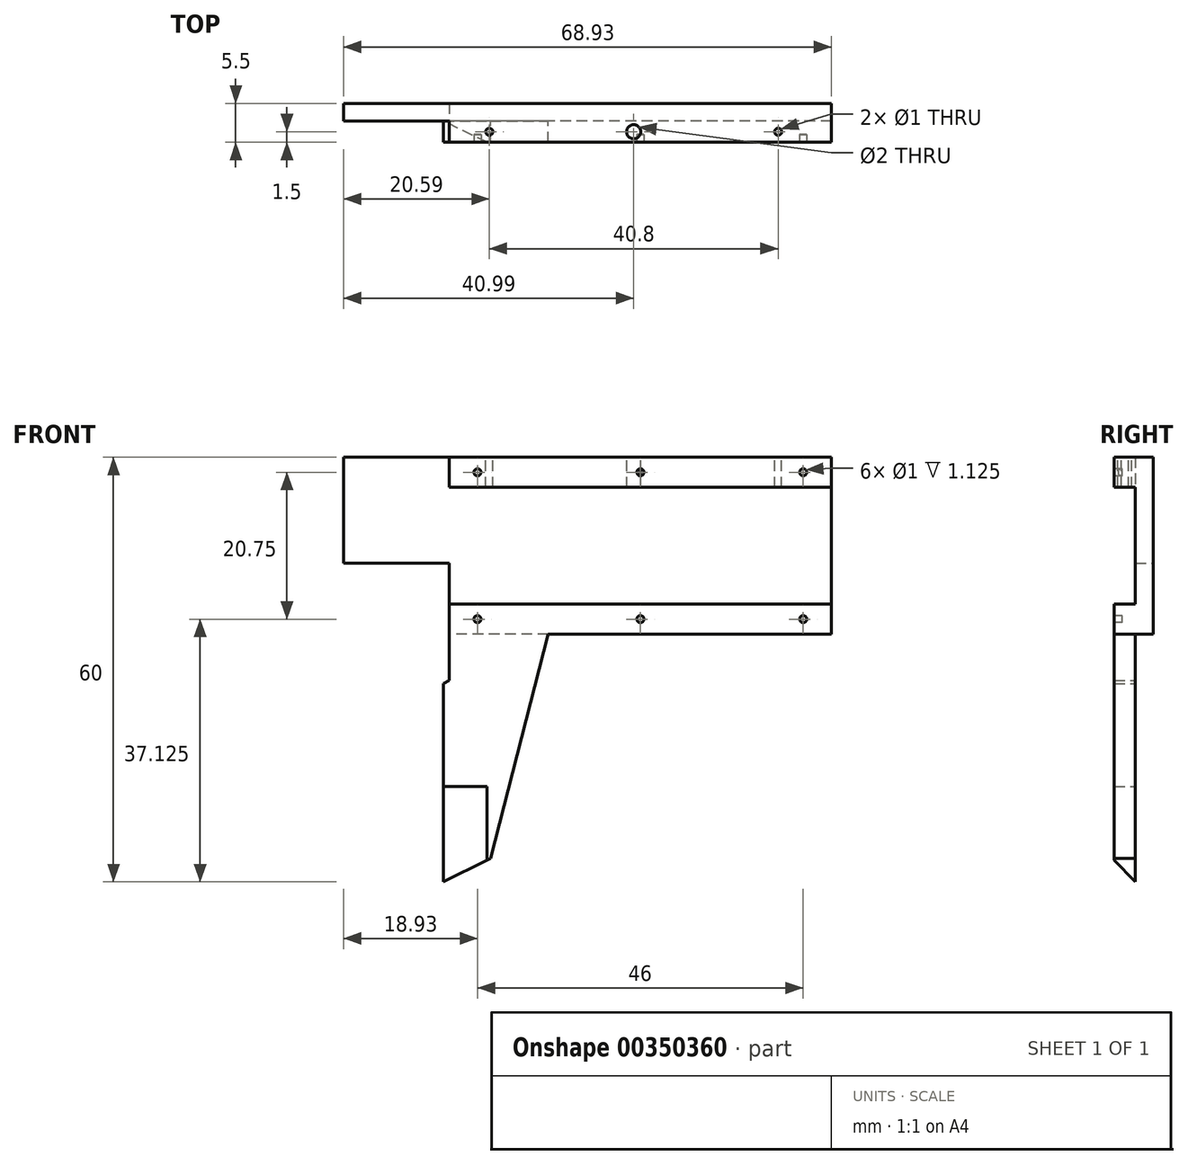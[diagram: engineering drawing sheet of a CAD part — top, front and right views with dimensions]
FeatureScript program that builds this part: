
annotation { "Feature Type Name" : "Feature", "Feature Type Description" : "" }
export const myFeature = defineFeature(function(context is Context, id is Id, definition is map)
    precondition{}
    {
        {
            var Q0;
            Q0=qCreatedBy(makeId("Front.planeOp"),FACE);
            var sketch = newSketch(context, id + "F0", { "sketchPlane" : qUnion([Q0])});
            skLineSegment(sketch, "E0", {"start": v(0, 0) * mm, "end": v(-55.4, 0) * mm, "construction": true});
            skLineSegment(sketch, "E1", {"start": v(0, 12.5) * mm, "end": v(0, -12.5) * mm});
            skLineSegment(sketch, "E2", {"start": v(0, -12.5) * mm, "end": v(-40, -12.5) * mm});
            skLineSegment(sketch, "E3", {"start": v(-40, -12.5) * mm, "end": v(-48.17, -44.18) * mm});
            skLineSegment(sketch, "E4", {"start": v(-48.17, -44.18) * mm, "end": v(-54.8, -47.5) * mm});
            skLineSegment(sketch, "E5", {"start": v(-54.8, -47.5) * mm, "end": v(-54.8, -19.5) * mm});
            skLineSegment(sketch, "E6", {"start": v(-54.8, -19.5) * mm, "end": v(-54, -19.04) * mm});
            skLineSegment(sketch, "E7", {"start": v(-54, -19.04) * mm, "end": v(-54, -2.5) * mm});
            skLineSegment(sketch, "E8", {"start": v(-54, -2.5) * mm, "end": v(-68.93, -2.5) * mm});
            skLineSegment(sketch, "E9", {"start": v(0, 12.5) * mm, "end": v(-68.93, 12.5) * mm});
            skLineSegment(sketch, "E10", {"start": v(-68.93, 12.5) * mm, "end": v(-68.93, -2.5) * mm});
            skSolve(sketch);
        }
        {
            var Q0;
            Q0=qSketchRegion(id+"F0",true);
            extrude(context, id + "F1", {"entities" : qUnion([Q0]), "depth" : 5.5 * mm});
        }
        {
            var Q0;
            Q0=makeQuery(id+"F1.opExtrude","CAP_FACE",FACE,{"disambiguationData":[OSD([sQuery(id+"F0.wireOp",EDGE,"E1"),sQuery(id+"F0.wireOp",EDGE,"E2"),sQuery(id+"F0.wireOp",EDGE,"E3"),sQuery(id+"F0.wireOp",EDGE,"E4"),sQuery(id+"F0.wireOp",EDGE,"E5"),sQuery(id+"F0.wireOp",EDGE,"E6"),sQuery(id+"F0.wireOp",EDGE,"E7"),sQuery(id+"F0.wireOp",EDGE,"E8"),sQuery(id+"F0.wireOp",EDGE,"ps4h69ml-JGIz-fiXX-pNhC-RlthW3Jydgdh"),sQuery(id+"F0.wireOp",EDGE,"E9"),sQuery(id+"F0.wireOp",EDGE,"95Vc8VKD-sbNP-E8sn-toB8-PwlkbplALVXU"),sQuery(id+"F0.wireOp",EDGE,"v8oIzNfV-Wtr4-p2Ou-QnUo-0IRdxmqncbtp"),sQuery(id+"F0.wireOp",EDGE,"jtS7aXSn-cF8S-vqdd-pwNP-jGzUUDwUnf9m"),sQuery(id+"F0.wireOp",EDGE,"i4UCeh58-nwjS-PbdF-TUSo-CF3E2kTPfbWW")])],"isStart":false});
            var sketch = newSketch(context, id + "F2", { "sketchPlane" : qUnion([Q0])});
            skLineSegment(sketch, "E11", {"start": v(0, 8.25) * mm, "end": v(0, -8.25) * mm});
            skLineSegment(sketch, "E12", {"start": v(0, -8.25) * mm, "end": v(-54, -8.25) * mm});
            skLineSegment(sketch, "E13", {"start": v(-54, -8.25) * mm, "end": v(-54, -2.5) * mm});
            skLineSegment(sketch, "E14", {"start": v(-54, -2.5) * mm, "end": v(-73.78, -2.5) * mm});
            skLineSegment(sketch, "E15", {"start": v(-73.78, -2.5) * mm, "end": v(-73.78, 31.93) * mm});
            skLineSegment(sketch, "E16", {"start": v(-73.78, 31.93) * mm, "end": v(-54, 31.93) * mm});
            skLineSegment(sketch, "E17", {"start": v(-54, 31.93) * mm, "end": v(-54, 8.25) * mm});
            skLineSegment(sketch, "E18", {"start": v(-54, 8.25) * mm, "end": v(0, 8.25) * mm});
            skSolve(sketch);
        }
        {
            var Q0;
            Q0=qSketchRegion(id+"F2",true);
            extrude(context, id + "F3", {"entities" : qUnion([Q0]), "operationType" : NewBodyOperationType.REMOVE, "oppositeDirection" : true, "depth" : 3 * mm});
        }
        {
            var Q0;
            {var subQ0=sQuery(id+"F0.wireOp",EDGE,"E1");var subQ1=sQuery(id+"F0.wireOp",EDGE,"E9");Q0=makeQuery(id+"F3.boolean.opBoolean","SPLIT",FACE,{"disambiguationData":[TD([makeQuery(id+"F1.opExtrude","SWEPT_FACE",FACE,{"disambiguationData":[OSD([subQ1])]})])],"derivedFrom":makeQuery(id+"F1.opExtrude","CAP_FACE",FACE,{"disambiguationData":[OSD([subQ0,sQuery(id+"F0.wireOp",EDGE,"E2"),sQuery(id+"F0.wireOp",EDGE,"E3"),sQuery(id+"F0.wireOp",EDGE,"E4"),sQuery(id+"F0.wireOp",EDGE,"E5"),sQuery(id+"F0.wireOp",EDGE,"E6"),sQuery(id+"F0.wireOp",EDGE,"E7"),sQuery(id+"F0.wireOp",EDGE,"E8"),sQuery(id+"F0.wireOp",EDGE,"ps4h69ml-JGIz-fiXX-pNhC-RlthW3Jydgdh"),subQ1,sQuery(id+"F0.wireOp",EDGE,"95Vc8VKD-sbNP-E8sn-toB8-PwlkbplALVXU"),sQuery(id+"F0.wireOp",EDGE,"v8oIzNfV-Wtr4-p2Ou-QnUo-0IRdxmqncbtp"),sQuery(id+"F0.wireOp",EDGE,"jtS7aXSn-cF8S-vqdd-pwNP-jGzUUDwUnf9m"),sQuery(id+"F0.wireOp",EDGE,"i4UCeh58-nwjS-PbdF-TUSo-CF3E2kTPfbWW")])],"isStart":false})});}
            var sketch = newSketch(context, id + "F4", { "sketchPlane" : qUnion([Q0])});
            skLineSegment(sketch, "E19", {"start": v(0, 0) * mm, "end": v(-25.2, 0) * mm, "construction": true});
            skCircle(sketch, "E20", {"center": v(-4, 10.38) * mm, "radius": 0.5 * mm});
            skCircle(sketch, "E21", {"center": v(-27, 10.38) * mm, "radius": 0.5 * mm});
            skCircle(sketch, "E22", {"center": v(-50, 10.37) * mm, "radius": 0.5 * mm});
            skCircle(sketch, "E23.MirrorC", {"center": v(-50, -10.38) * mm, "radius": 0.5 * mm});
            skCircle(sketch, "E24.MirrorC", {"center": v(-27, -10.38) * mm, "radius": 0.5 * mm});
            skCircle(sketch, "E25.MirrorC", {"center": v(-4, -10.38) * mm, "radius": 0.5 * mm});
            skSolve(sketch);
        }
        {
            var Q0;
            Q0=qSketchRegion(id+"F4",true);
            extrude(context, id + "F5", {"entities" : qUnion([Q0]), "operationType" : NewBodyOperationType.REMOVE, "oppositeDirection" : true, "depth" : 1.12 * mm});
        }
        {
            var Q0;
            Q0=makeQuery(id+"F1.opExtrude","SWEPT_FACE",FACE,{"disambiguationData":[OSD([sQuery(id+"F0.wireOp",EDGE,"E9")])]});
            cPlane(context, id + "F6", {"entities" : qUnion([Q0]), "cplaneType" : CPlaneType.OFFSET, "offset" : 17.5 * mm, "width" : 150 * mm, "height" : 150 * mm});
        }
        {
            var Q0;
            Q0=makeQuery(id+"F1.opExtrude","SWEPT_FACE",FACE,{"disambiguationData":[OSD([sQuery(id+"F0.wireOp",EDGE,"E2")])]});
            var Q1;
            Q1=makeQuery(id+"F1.opExtrude","CAP_VERTEX",VERTEX,{"disambiguationData":[OSD([sQuery(id+"F0.wireOp",EDGE,"E4"),sQuery(id+"F0.wireOp",EDGE,"E5")])],"isStart":false});
            cPlane(context, id + "F7", {"entities" : qUnion([Q0, Q1]), "cplaneType" : CPlaneType.PLANE_POINT, "offset" : 34.75 * mm, "width" : 150 * mm, "height" : 150 * mm});
        }
        {
            var Q0;
            Q0=qCreatedBy(id+"F6.planeOp",FACE);
            var sketch = newSketch(context, id + "F8", { "sketchPlane" : qUnion([Q0])});
            skLineSegment(sketch, "E26.0", {"start": v(-62, -2.5) * mm, "end": v(-62, 0) * mm});
            skLineSegment(sketch, "E27", {"start": v(-62, 0) * mm, "end": v(-67.13, 0) * mm});
            skLineSegment(sketch, "E28", {"start": v(-67.13, 0) * mm, "end": v(-62, -2.5) * mm});
            skLineSegment(sketch, "E29", {"start": v(-62, -1.25) * mm, "end": v(-70.99, -1.25) * mm, "construction": true});
            skLineSegment(sketch, "E30.MirrorCS", {"start": v(-62, 0) * mm, "end": v(-62, -2.5) * mm});
            skSolve(sketch);
        }
        {
            var Q0;
            Q0=qSketchRegion(id+"F8",true);
            extrude(context, id + "F9", {"entities" : qUnion([Q0]), "operationType" : NewBodyOperationType.REMOVE, "oppositeDirection" : true, "depth" : 12.5 * mm});
        }
        {
            var Q0;
            Q0=makeQuery(id+"F1.opExtrude","SWEPT_FACE",FACE,{"disambiguationData":[OSD([sQuery(id+"F0.wireOp",EDGE,"E2")])]});
            var sketch = newSketch(context, id + "F10", { "sketchPlane" : qUnion([Q0])});
            skLineSegment(sketch, "E31.bottom", {"start": v(-40, 0) * mm, "end": v(-54.8, 0) * mm});
            skLineSegment(sketch, "E31.top", {"start": v(-40, 2.5) * mm, "end": v(-54.8, 2.5) * mm});
            skLineSegment(sketch, "E31.left", {"start": v(-40, 0) * mm, "end": v(-40, 2.5) * mm});
            skLineSegment(sketch, "E31.right", {"start": v(-54.8, 0) * mm, "end": v(-54.8, 2.5) * mm});
            skSolve(sketch);
        }
        {
            var Q0;
            Q0=qSketchRegion(id+"F10",true);
            extrude(context, id + "F11", {"entities" : qUnion([Q0]), "operationType" : NewBodyOperationType.REMOVE, "depth" : 47 * mm});
        }
        {
            var Q0;
            Q0=qCreatedBy(id+"F7.planeOp",FACE);
            var sketch = newSketch(context, id + "F12", { "sketchPlane" : qUnion([Q0])});
            skLineSegment(sketch, "E32.0", {"start": v(-54.8, 5.5) * mm, "end": v(-54.8, 2.5) * mm});
            skLineSegment(sketch, "E33", {"start": v(-54.8, 5.5) * mm, "end": v(-48.65, 5.5) * mm});
            skLineSegment(sketch, "E34", {"start": v(-48.65, 5.5) * mm, "end": v(-54.8, 2.5) * mm});
            skSolve(sketch);
        }
        {
            var Q0;
            Q0=qSketchRegion(id+"F12",true);
            extrude(context, id + "F13", {"entities" : qUnion([Q0]), "operationType" : NewBodyOperationType.REMOVE, "oppositeDirection" : true, "depth" : 13.5 * mm});
        }
        {
            var Q0;
            Q0=makeQuery(id+"F1.opExtrude","SWEPT_FACE",FACE,{"disambiguationData":[OSD([sQuery(id+"F0.wireOp",EDGE,"E9")])]});
            var sketch = newSketch(context, id + "F14", { "sketchPlane" : qUnion([Q0])});
            skCircle(sketch, "E35", {"center": v(-7.54, -4) * mm, "radius": 0.5 * mm});
            skCircle(sketch, "E36", {"center": v(-48.34, -4) * mm, "radius": 0.5 * mm});
            skSolve(sketch);
        }
        {
            var Q0;
            Q0=qSketchRegion(id+"F14",true);
            extrude(context, id + "F15", {"entities" : qUnion([Q0]), "operationType" : NewBodyOperationType.REMOVE, "endBound" : BoundingType.UP_TO_NEXT, "oppositeDirection" : true, "depth" : 3 * mm});
        }
        {
            var Q0;
            Q0=makeQuery(id+"F1.opExtrude","SWEPT_FACE",FACE,{"disambiguationData":[OSD([sQuery(id+"F0.wireOp",EDGE,"E9")])]});
            var sketch = newSketch(context, id + "F16", { "sketchPlane" : qUnion([Q0])});
            skCircle(sketch, "E37", {"center": v(-27.94, -4) * mm, "radius": 1 * mm});
            skPoint(sketch, "E38", {"position": v(-7.54, -4) * mm});
            skSolve(sketch);
        }
        {
            var Q0;
            Q0=qSketchRegion(id+"F16",true);
            extrude(context, id + "F17", {"entities" : qUnion([Q0]), "operationType" : NewBodyOperationType.REMOVE, "endBound" : BoundingType.UP_TO_NEXT, "oppositeDirection" : true, "depth" : 25 * mm});
        }
    });
